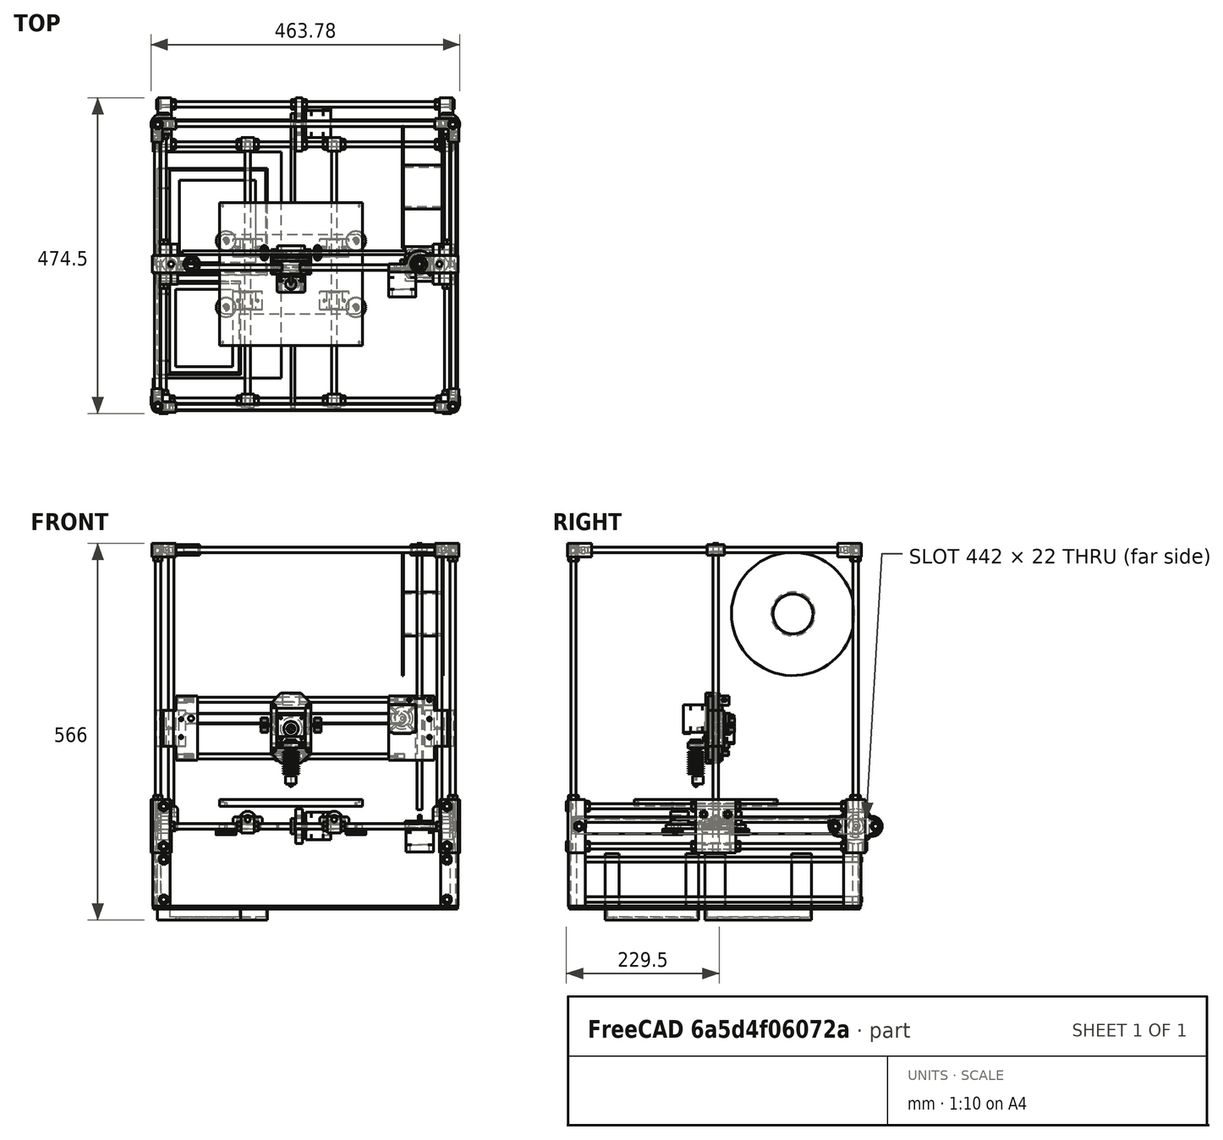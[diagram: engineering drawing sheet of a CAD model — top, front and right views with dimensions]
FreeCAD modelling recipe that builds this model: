
FCSTD DOCUMENT  (FreeCAD 0.16R6707 (Git))
Label: 3DPrinter
License: All rights reserved
LicenseURL: http://en.wikipedia.org/wiki/All_rights_reserved
objects: Part::Feature×127, Sketcher::SketchObject×20, PartDesign::Pad×20, Part::MultiFuse×16
note: 203 computed .brp shape members not serialized (recipe doc carries the construction recipe); baked Part::Feature solids carry a one-line shape summary decoded from their .brp

FEATURE [Sketcher::SketchObject] Sketch
  Placement = pos=(0,0,0) rot=(1,0,0;1.5708rad)
  sketch-geometry (2):
    g0: Circle CenterX=-65 CenterY=0 CenterZ=0 NormalX=0 NormalY=0 NormalZ=1 Radius=4
    g1: Circle CenterX=65 CenterY=0 CenterZ=0 NormalX=0 NormalY=0 NormalZ=1 Radius=4
  constraints (6):
    c: PointOnObject(g1,g-1)
    c: PointOnObject(g0,g-1)
    c: Radius(g0) = 4
    c: Equal(g0,g1)
    c: DistanceX(g0,g1) = 130
    c: Symmetric(g0,g1,g-2)
FEATURE [PartDesign::Pad] Pad  label="Rods"
  Length = 400
  Length2 = 100
  Midplane = true
  Placement = pos=(0,0,0) rot=(1,0,0;1.5708rad)
  Sketch = -> Sketch
  Type = 0
FEATURE [Sketcher::SketchObject] Sketch001
  Placement = pos=(0,0,-13.5) rot=(0,0,1;0rad)
  sketch-geometry (36):
    g0: LineSegment StartX=-97.5 StartY=60 StartZ=0 EndX=97.5 EndY=60 EndZ=0
    g1: LineSegment StartX=107.5 StartY=50 StartZ=0 EndX=107.5 EndY=-50 EndZ=0
    g2: LineSegment StartX=97.5 StartY=-60 StartZ=0 EndX=-97.5 EndY=-60 EndZ=0
    g3: LineSegment StartX=-107.5 StartY=-50 StartZ=0 EndX=-107.5 EndY=50 EndZ=0
    g4: ArcOfCircle CenterX=-97.5 CenterY=50 CenterZ=0 NormalX=0 NormalY=0 NormalZ=1 Radius=10 StartAngle=1.57079 EndAngle=3.14159
    g5: ArcOfCircle CenterX=97.5 CenterY=50 CenterZ=0 NormalX=0 NormalY=0 NormalZ=1 Radius=9.99998 StartAngle=6.28319 EndAngle=7.85398
    g6: ArcOfCircle CenterX=97.5 CenterY=-50 CenterZ=0 NormalX=0 NormalY=0 NormalZ=1 Radius=10 StartAngle=4.71239 EndAngle=6.28319
    g7: ArcOfCircle CenterX=-97.5 CenterY=-50 CenterZ=0 NormalX=0 NormalY=0 NormalZ=1 Radius=10 StartAngle=3.14159 EndAngle=4.71239
    g8: ArcOfCircle CenterX=-82.5 CenterY=40 CenterZ=0 NormalX=0 NormalY=0 NormalZ=1 Radius=1.8 StartAngle=1.5708 EndAngle=4.71239
    g9: ArcOfCircle CenterX=-77.5 CenterY=40 CenterZ=0 NormalX=0 NormalY=0 NormalZ=1 Radius=1.8 StartAngle=4.71239 EndAngle=7.85398
    g10: LineSegment StartX=-82.5 StartY=38.2 StartZ=0 EndX=-77.5 EndY=38.2 EndZ=0
    g11: LineSegment StartX=-82.5 StartY=41.8 StartZ=0 EndX=-77.5 EndY=41.8 EndZ=0
    g12: ArcOfCircle CenterX=-52.5 CenterY=40 CenterZ=0 NormalX=0 NormalY=0 NormalZ=1 Radius=1.8 StartAngle=1.5708 EndAngle=4.71239
    g13: ArcOfCircle CenterX=-47.5 CenterY=40 CenterZ=0 NormalX=0 NormalY=0 NormalZ=1 Radius=1.8 StartAngle=4.71239 EndAngle=7.85398
    g14: LineSegment StartX=-52.5 StartY=38.2 StartZ=0 EndX=-47.5 EndY=38.2 EndZ=0
    g15: LineSegment StartX=-52.5 StartY=41.8 StartZ=0 EndX=-47.5 EndY=41.8 EndZ=0
    g16: ArcOfCircle CenterX=47.5 CenterY=40 CenterZ=0 NormalX=0 NormalY=0 NormalZ=1 Radius=1.8 StartAngle=1.5708 EndAngle=4.71239
    g17: ArcOfCircle CenterX=52.5 CenterY=40 CenterZ=0 NormalX=0 NormalY=0 NormalZ=1 Radius=1.8 StartAngle=4.71239 EndAngle=7.85398
    g18: LineSegment StartX=47.5 StartY=38.2 StartZ=0 EndX=52.5 EndY=38.2 EndZ=0
    g19: LineSegment StartX=47.5 StartY=41.8 StartZ=0 EndX=52.5 EndY=41.8 EndZ=0
    g20: ArcOfCircle CenterX=77.5 CenterY=40 CenterZ=0 NormalX=0 NormalY=0 NormalZ=1 Radius=1.8 StartAngle=1.5708 EndAngle=4.71239
    g21: ArcOfCircle CenterX=82.5 CenterY=40 CenterZ=0 NormalX=0 NormalY=0 NormalZ=1 Radius=1.8 StartAngle=4.71239 EndAngle=7.85398
    g22: LineSegment StartX=77.5 StartY=38.2 StartZ=0 EndX=82.5 EndY=38.2 EndZ=0
    g23: LineSegment StartX=77.5 StartY=41.8 StartZ=0 EndX=82.5 EndY=41.8 EndZ=0
    g24: Circle CenterX=-80 CenterY=-40 CenterZ=0 NormalX=0 NormalY=0 NormalZ=1 Radius=1.8
    g25: Circle CenterX=-50 CenterY=-40 CenterZ=0 NormalX=0 NormalY=0 NormalZ=1 Radius=1.8
    g26: Circle CenterX=50 CenterY=-40 CenterZ=0 NormalX=0 NormalY=0 NormalZ=1 Radius=1.8
    g27: Circle CenterX=80 CenterY=-40 CenterZ=0 NormalX=0 NormalY=0 NormalZ=1 Radius=1.8
    g28: Circle CenterX=-97.5 CenterY=-50 CenterZ=0 NormalX=0 NormalY=0 NormalZ=1 Radius=1.8
    g29: Circle CenterX=-97.5 CenterY=50 CenterZ=0 NormalX=0 NormalY=0 NormalZ=1 Radius=1.8
    g30: Circle CenterX=97.5 CenterY=50 CenterZ=0 NormalX=0 NormalY=0 NormalZ=1 Radius=1.8
    g31: Circle CenterX=97.5 CenterY=-50 CenterZ=0 NormalX=0 NormalY=0 NormalZ=1 Radius=1.8
    g32: Circle CenterX=-20 CenterY=20 CenterZ=0 NormalX=0 NormalY=0 NormalZ=1 Radius=1.8
    g33: Circle CenterX=20 CenterY=20 CenterZ=0 NormalX=0 NormalY=0 NormalZ=1 Radius=1.8
    g34: Circle CenterX=-20 CenterY=-20 CenterZ=0 NormalX=0 NormalY=0 NormalZ=1 Radius=1.8
    g35: Circle CenterX=20 CenterY=-20 CenterZ=0 NormalX=0 NormalY=0 NormalZ=1 Radius=1.8
  constraints (95):
    c: Horizontal(g2)
    c: Vertical(g1)
    c: Vertical(g3)
    c: DistanceX(g0,g0) = 195
    c: DistanceY(g3,g3) = 100
    c: Symmetric(g0,g0,g-2)
    c: Symmetric(g2,g0,g-1)
    c: Coincident(g7,g3)
    c: Coincident(g7,g2)
    c: Coincident(g3,g4)
    c: Coincident(g4,g0)
    c: Coincident(g0,g5)
    c: Coincident(g5,g1)
    c: Coincident(g1,g6)
    c: Coincident(g6,g2)
    c: Tangent(g6,g1)
    c: Tangent(g5,g1)
    c: Tangent(g5,g0)
    c: Tangent(g2,g7)
    c: Tangent(g7,g3)
    c: Tangent(g3,g4)
    c: Tangent(g4,g0)
    c: Tangent(g6,g2)
    c: Equal(g4,g7)
    c: Equal(g7,g6)
    c: Radius(g4) = 10
    c: Tangent(g8,g11) = 1.5708
    c: Tangent(g8,g10) = -1.5708
    c: Tangent(g10,g9) = -1.5708
    c: Tangent(g11,g9) = 1.5708
    c: Horizontal(g10)
    c: Equal(g8,g9)
    c: Tangent(g12,g15) = 1.5708
    c: Tangent(g12,g14) = -1.5708
    c: Tangent(g14,g13) = -1.5708
    c: Tangent(g15,g13) = 1.5708
    c: Horizontal(g14)
    c: Equal(g12,g13)
    c: Tangent(g16,g19) = 1.5708
    c: Tangent(g16,g18) = -1.5708
    c: Tangent(g18,g17) = -1.5708
    c: Tangent(g19,g17) = 1.5708
    c: Horizontal(g18)
    c: Equal(g16,g17)
    c: Tangent(g20,g23) = 1.5708
    c: Tangent(g20,g22) = -1.5708
    c: Tangent(g22,g21) = -1.5708
    c: Tangent(g23,g21) = 1.5708
    c: Horizontal(g22)
    c: Equal(g20,g21)
    c: Radius(g24) = 1.8
    c: Equal(g24,g25)
    c: Equal(g24,g26)
    c: Equal(g24,g27)
    c: Equal(g24,g20)
    c: Equal(g24,g16)
    c: Equal(g24,g12)
    c: Equal(g24,g8)
    c: DistanceY(g25,g24) = 0
    c: DistanceY(g26,g25) = 0
    c: DistanceY(g26,g27) = 0
    c: DistanceY(g20,g17) = 0
    c: DistanceY(g16,g13) = 0
    c: DistanceY(g9,g12) = 0
    c: Symmetric(g13,g16,g-2)
    c: Symmetric(g25,g26,g-2)
    c: DistanceX(g24,g25) = 30
    c: DistanceX(g26,g27) = 30
    c: DistanceX(g25,g26) = 100
    c: DistanceX(g17,g20) = 25
    c: DistanceX(g16,g21) = 35
    c: Equal(g19,g23)
    c: Equal(g23,g15)
    c: Equal(g15,g11)
    c: DistanceX(g9,g12) = 25
    c: DistanceY(g8,g0) = 20
    c: DistanceY(g2,g24) = 20
    c: DistanceX(g13,g16) = 95
    c: Radius(g31) = 1.8
    c: Equal(g31,g30)
    c: Equal(g31,g29)
    c: Equal(g31,g28)
    c: Coincident(g28,g7)
    c: Coincident(g29,g4)
    c: Coincident(g30,g5)
    c: Coincident(g31,g6)
    c: Radius(g32) = 1.8
    c: Equal(g32,g33)
    c: Equal(g32,g34)
    c: Equal(g32,g35)
    c: Symmetric(g32,g33,g-2)
    c: Symmetric(g33,g35,g-1)
    c: Symmetric(g34,g32,g-1)
    c: DistanceX(g32,g33) = 40
    c: DistanceY(g34,g32) = 40
FEATURE [PartDesign::Pad] Pad001  label="Y-Base"
  Length = 6
  Length2 = 100
  Placement = pos=(0,0,-13.5) rot=(0,0,1;0rad)
  Sketch = -> Sketch001
  Type = 0
FEATURE [Part::Feature] Part__Feature  label="BearingMount001"
  Placement = pos=(65,-26,0) rot=(1,0,0;1.5708rad)
  shape: bbox 43.69 x 27 x 12.5 mm, 30 faces (baked)
FEATURE [Part::Feature] Part__Feature001  label="BearingMount002"
  Placement = pos=(65,53,0) rot=(1,0,0;1.5708rad)
  shape: bbox 43.69 x 27 x 12.5 mm, 30 faces (baked)
FEATURE [Part::Feature] Part__Feature002  label="BearingMount003"
  Placement = pos=(-65,-26,0) rot=(1,0,0;1.5708rad)
  shape: bbox 43.69 x 27 x 12.5 mm, 30 faces (baked)
FEATURE [Part::Feature] Part__Feature003  label="BearingMount004"
  Placement = pos=(-65,53,0) rot=(1,0,0;1.5708rad)
  shape: bbox 43.69 x 27 x 12.5 mm, 30 faces (baked)
FEATURE [Sketcher::SketchObject] Sketch002
  Placement = pos=(0,0,20) rot=(0,0,1;0rad)
  sketch-geometry (8):
    g0: LineSegment StartX=-107.5 StartY=107.5 StartZ=0 EndX=107.5 EndY=107.5 EndZ=0
    g1: LineSegment StartX=107.5 StartY=107.5 StartZ=0 EndX=107.5 EndY=-107.5 EndZ=0
    g2: LineSegment StartX=107.5 StartY=-107.5 StartZ=0 EndX=-107.5 EndY=-107.5 EndZ=0
    g3: LineSegment StartX=-107.5 StartY=-107.5 StartZ=0 EndX=-107.5 EndY=107.5 EndZ=0
    g4: Circle CenterX=-97.5 CenterY=-50 CenterZ=0 NormalX=0 NormalY=0 NormalZ=1 Radius=1.8
    g5: Circle CenterX=-97.5 CenterY=50 CenterZ=0 NormalX=0 NormalY=0 NormalZ=1 Radius=1.8
    g6: Circle CenterX=97.5 CenterY=-50 CenterZ=0 NormalX=0 NormalY=0 NormalZ=1 Radius=1.8
    g7: Circle CenterX=97.5 CenterY=50 CenterZ=0 NormalX=0 NormalY=0 NormalZ=1 Radius=1.8
  constraints (21):
    c: Coincident(g0,g1)
    c: Coincident(g1,g2)
    c: Coincident(g2,g3)
    c: Coincident(g3,g0)
    c: Horizontal(g0)
    c: Horizontal(g2)
    c: Vertical(g1)
    c: Vertical(g3)
    c: Symmetric(g1,g2,g-2)
    c: Symmetric(g0,g1,g-1)
    c: Equal(g1,g0)
    c: DistanceY(g1,g1) = 215
    c: Radius(g7) = 1.8
    c: Equal(g7,g6)
    c: Equal(g7,g5)
    c: Equal(g7,g4)
    c: Symmetric(g5,g7,g-2)
    c: Symmetric(g5,g4,g-1)
    c: Symmetric(g7,g6,g-1)
    c: DistanceX(g5,g7) = 195
    c: DistanceY(g4,g5) = 100
FEATURE [Part::Feature] Part__Feature004  label="BearingBase001"
  Placement = pos=(65,-53,0) rot=(-1,0,0;1.5708rad)
  shape: bbox 43.69 x 27 x 7.5 mm, 26 faces (baked)
FEATURE [Part::Feature] Part__Feature005  label="BearingBase002"
  Placement = pos=(65,26,0) rot=(-1,0,0;1.5708rad)
  shape: bbox 43.69 x 27 x 7.5 mm, 26 faces (baked)
FEATURE [Part::Feature] Part__Feature006  label="BearingBase003"
  Placement = pos=(-65,-53,0) rot=(-1,0,0;1.5708rad)
  shape: bbox 43.69 x 27 x 7.5 mm, 26 faces (baked)
FEATURE [Part::Feature] Part__Feature007  label="BearingBase004"
  Placement = pos=(-65,26,0) rot=(-1,0,0;1.5708rad)
  shape: bbox 43.69 x 27 x 7.5 mm, 26 faces (baked)
FEATURE [Part::MultiFuse] Fusion  label="BearingMount"
  Shapes = -> [Part__Feature007,Part__Feature,Part__Feature001,Part__Feature002,Part__Feature003,Part__Feature004,Part__Feature005,Part__Feature006]
FEATURE [PartDesign::Pad] Pad002  label="PrintingBedBase"
  Length = 5
  Length2 = 100
  Placement = pos=(0,0,20) rot=(0,0,1;0rad)
  Sketch = -> Sketch002
  Type = 0
FEATURE [Sketcher::SketchObject] Sketch003
  Placement = pos=(0,0,25) rot=(0,0,1;0rad)
  sketch-geometry (4):
    g0: LineSegment StartX=-107.5 StartY=107.5 StartZ=0 EndX=107.5 EndY=107.5 EndZ=0
    g1: LineSegment StartX=107.5 StartY=107.5 StartZ=0 EndX=107.5 EndY=-107.5 EndZ=0
    g2: LineSegment StartX=107.5 StartY=-107.5 StartZ=0 EndX=-107.5 EndY=-107.5 EndZ=0
    g3: LineSegment StartX=-107.5 StartY=-107.5 StartZ=0 EndX=-107.5 EndY=107.5 EndZ=0
  constraints (12):
    c: Coincident(g0,g1)
    c: Coincident(g1,g2)
    c: Coincident(g2,g3)
    c: Coincident(g3,g0)
    c: Horizontal(g0)
    c: Horizontal(g2)
    c: Vertical(g1)
    c: Vertical(g3)
    c: Symmetric(g1,g2,g-2)
    c: Symmetric(g0,g1,g-1)
    c: Equal(g1,g0)
    c: DistanceY(g1,g1) = 215
FEATURE [PartDesign::Pad] Pad003  label="Insulation"
  Length = 1
  Length2 = 100
  Placement = pos=(0,0,25) rot=(0,0,1;0rad)
  Sketch = -> Sketch003
  Type = 0
FEATURE [Sketcher::SketchObject] Sketch004
  Placement = pos=(0,0,26) rot=(0,0,1;0rad)
  sketch-geometry (8):
    g0: LineSegment StartX=-107.5 StartY=107.5 StartZ=0 EndX=107.5 EndY=107.5 EndZ=0
    g1: LineSegment StartX=107.5 StartY=107.5 StartZ=0 EndX=107.5 EndY=-107.5 EndZ=0
    g2: LineSegment StartX=107.5 StartY=-107.5 StartZ=0 EndX=-107.5 EndY=-107.5 EndZ=0
    g3: LineSegment StartX=-107.5 StartY=-107.5 StartZ=0 EndX=-107.5 EndY=107.5 EndZ=0
    g4: Circle CenterX=-102.5 CenterY=-102.5 CenterZ=0 NormalX=0 NormalY=0 NormalZ=1 Radius=1.3
    g5: Circle CenterX=-102.5 CenterY=102.5 CenterZ=0 NormalX=0 NormalY=0 NormalZ=1 Radius=1.3
    g6: Circle CenterX=102.5 CenterY=102.5 CenterZ=0 NormalX=0 NormalY=0 NormalZ=1 Radius=1.3
    g7: Circle CenterX=102.5 CenterY=-102.5 CenterZ=0 NormalX=0 NormalY=0 NormalZ=1 Radius=1.3
  constraints (21):
    c: Coincident(g0,g1)
    c: Coincident(g1,g2)
    c: Coincident(g2,g3)
    c: Coincident(g3,g0)
    c: Horizontal(g0)
    c: Horizontal(g2)
    c: Vertical(g1)
    c: Vertical(g3)
    c: Symmetric(g1,g2,g-2)
    c: Symmetric(g0,g1,g-1)
    c: Equal(g1,g0)
    c: DistanceY(g1,g1) = 215
    c: Radius(g5) = 1.3
    c: Equal(g5,g6)
    c: Equal(g5,g7)
    c: Equal(g5,g4)
    c: Symmetric(g4,g7,g-2)
    c: Symmetric(g7,g6,g-1)
    c: Symmetric(g5,g4,g-1)
    c: DistanceX(g5,g6) = 205
    c: DistanceY(g4,g5) = 205
FEATURE [PartDesign::Pad] Pad004  label="HeatBed"
  Length = 1
  Length2 = 100
  Placement = pos=(0,0,26) rot=(0,0,1;0rad)
  Sketch = -> Sketch004
  Type = 0
FEATURE [Sketcher::SketchObject] Sketch005
  Placement = pos=(0,0,27) rot=(0,0,1;0rad)
  sketch-geometry (4):
    g0: LineSegment StartX=-107.5 StartY=107.5 StartZ=0 EndX=107.5 EndY=107.5 EndZ=0
    g1: LineSegment StartX=107.5 StartY=107.5 StartZ=0 EndX=107.5 EndY=-107.5 EndZ=0
    g2: LineSegment StartX=107.5 StartY=-107.5 StartZ=0 EndX=-107.5 EndY=-107.5 EndZ=0
    g3: LineSegment StartX=-107.5 StartY=-107.5 StartZ=0 EndX=-107.5 EndY=107.5 EndZ=0
  constraints (12):
    c: Coincident(g0,g1)
    c: Coincident(g1,g2)
    c: Coincident(g2,g3)
    c: Coincident(g3,g0)
    c: Horizontal(g0)
    c: Horizontal(g2)
    c: Vertical(g1)
    c: Vertical(g3)
    c: Symmetric(g1,g2,g-2)
    c: Symmetric(g0,g1,g-1)
    c: Equal(g1,g0)
    c: DistanceY(g1,g1) = 215
FEATURE [PartDesign::Pad] Pad005  label="GlassPrintingBed"
  Length = 3
  Length2 = 100
  Placement = pos=(0,0,27) rot=(0,0,1;0rad)
  Sketch = -> Sketch005
  Type = 0
FEATURE [Part::Feature] Part__Feature008  label="HeightKnob001"
  Placement = pos=(97.5,-50,-22.5) rot=(0,0,1;0rad)
  shape: bbox 30 x 29.93 x 9 mm, 135 faces (baked)
FEATURE [Part::Feature] Part__Feature009  label="HeightKnob002"
  Placement = pos=(97.5,50,-22.5) rot=(0,0,1;0rad)
  shape: bbox 30 x 29.93 x 9 mm, 135 faces (baked)
FEATURE [Part::Feature] Part__Feature010  label="HeightKnob003"
  Placement = pos=(-97.5,-50,-22.5) rot=(0,0,1;0rad)
  shape: bbox 30 x 29.93 x 9 mm, 135 faces (baked)
FEATURE [Part::Feature] Part__Feature011  label="HeightKnob004"
  Placement = pos=(-97.5,50,-22.5) rot=(0,0,1;0rad)
  shape: bbox 30 x 29.93 x 9 mm, 135 faces (baked)
FEATURE [Part::MultiFuse] Fusion001  label="HeightKnob"
  Shapes = -> [Part__Feature008,Part__Feature009,Part__Feature010,Part__Feature011]
FEATURE [Part::MultiFuse] Fusion002  label="Y-Axis"
  Placement = pos=(0,0,15) rot=(0,0,1;0rad)
  Shapes = -> [Pad,Pad001,Fusion,Pad002,Pad003,Pad004,Pad005,Fusion001]
FEATURE [Part::Feature] Part__Feature012  label="Nema17"
  Placement = pos=(20.5,42.5,72) rot=(0,0.707107,-0.707107;3.14159rad)
  shape: bbox 41 x 55.5 x 43 mm, 73 faces (baked)
FEATURE [Part::Feature] Part__Feature013  label="Nema17_X"
  Placement = pos=(146.5,-34,87.5) rot=(-1,0,0;1.5708rad)
  shape: bbox 41 x 55.5 x 43 mm, 73 faces (baked)
FEATURE [Sketcher::SketchObject] Sketch006
  Placement = pos=(0,35,10) rot=(1,0,0;1.5708rad)
  sketch-geometry (20):
    g0: ArcOfCircle CenterX=-155 CenterY=57 CenterZ=0 NormalX=0 NormalY=0 NormalZ=1 Radius=7 StartAngle=1.5708 EndAngle=4.71239
    g1: ArcOfCircle CenterX=165 CenterY=57 CenterZ=0 NormalX=0 NormalY=0 NormalZ=1 Radius=7 StartAngle=4.71239 EndAngle=7.85398
    g2: LineSegment StartX=-155 StartY=64 StartZ=0 EndX=165 EndY=64 EndZ=0
    g3: ArcOfCircle CenterX=-155 CenterY=57 CenterZ=0 NormalX=0 NormalY=0 NormalZ=1 Radius=8 StartAngle=1.5708 EndAngle=4.71239
    g4: ArcOfCircle CenterX=165 CenterY=57 CenterZ=0 NormalX=0 NormalY=0 NormalZ=1 Radius=8 StartAngle=4.71239 EndAngle=7.85398
    g5: LineSegment StartX=-155 StartY=65 StartZ=0 EndX=165 EndY=65 EndZ=0
    g6: LineSegment StartX=165 StartY=50 StartZ=0 EndX=33.8479 EndY=50 EndZ=0
    g7: LineSegment StartX=33.8479 StartY=50 StartZ=0 EndX=33.8479 EndY=44 EndZ=0
    g8: LineSegment StartX=33.8479 StartY=44 StartZ=0 EndX=45.4113 EndY=44 EndZ=0
    g9: LineSegment StartX=45.4113 StartY=44 StartZ=0 EndX=45.4113 EndY=45 EndZ=0
    g10: LineSegment StartX=45.4113 StartY=45 StartZ=0 EndX=34.8479 EndY=45 EndZ=0
    g11: LineSegment StartX=34.8479 StartY=45 StartZ=0 EndX=34.8479 EndY=49 EndZ=0
    g12: LineSegment StartX=34.8479 StartY=49 StartZ=0 EndX=165 EndY=49 EndZ=0
    g13: LineSegment StartX=-155 StartY=50 StartZ=0 EndX=-33.8479 EndY=50 EndZ=0
    g14: LineSegment StartX=-34.8479 StartY=49 StartZ=0 EndX=-155 EndY=49 EndZ=0
    g15: LineSegment StartX=-33.8479 StartY=50 StartZ=0 EndX=-33.8479 EndY=44 EndZ=0
    g16: LineSegment StartX=-33.8479 StartY=44 StartZ=0 EndX=-45.4113 EndY=44 EndZ=0
    g17: LineSegment StartX=-45.4113 StartY=44 StartZ=0 EndX=-45.4113 EndY=45 EndZ=0
    g18: LineSegment StartX=-45.4113 StartY=45 StartZ=0 EndX=-34.8479 EndY=45 EndZ=0
    g19: LineSegment StartX=-34.8479 StartY=45 StartZ=0 EndX=-34.8479 EndY=49 EndZ=0
  constraints (56):
    c: Tangent(g0,g2) = 1.5708
    c: Tangent(g2,g1) = 1.5708
    c: Equal(g0,g1)
    c: Tangent(g3,g5) = 1.5708
    c: Tangent(g5,g4) = 1.5708
    c: Equal(g3,g4)
    c: Coincident(g1,g4)
    c: Coincident(g0,g3)
    c: Radius(g0) = 7
    c: Radius(g3) = 8
    c: DistanceY(g-1,g0) = 57
    c: DistanceX(g0,g1) = 320
    c: Horizontal(g6)
    c: Coincident(g6,g7)
    c: Vertical(g7)
    c: Coincident(g7,g8)
    c: Horizontal(g8)
    c: Coincident(g8,g9)
    c: Coincident(g9,g10)
    c: Horizontal(g10)
    c: Coincident(g10,g11)
    c: Vertical(g11)
    c: Coincident(g11,g12)
    c: Horizontal(g12)
    c: Vertical(g9)
    c: Coincident(g12,g4)
    c: Coincident(g6,g1)
    c: DistanceX(g6,g11) = 1
    c: DistanceY(g-1,g1) = 57
    c: Horizontal(g13)
    c: Horizontal(g14)
    c: Coincident(g13,g0)
    c: Coincident(g14,g3)
    c: Symmetric(g3,g3,g0)
    c: Symmetric(g0,g0,g0)
    c: Vertical(g15)
    c: Coincident(g15,g16)
    c: Coincident(g16,g17)
    c: Vertical(g17)
    c: Coincident(g17,g18)
    c: Horizontal(g18)
    c: Coincident(g18,g19)
    c: Vertical(g19)
    c: Horizontal(g16)
    c: Coincident(g19,g14)
    c: Coincident(g15,g13)
    c: DistanceX(g14,g13) = 1
    c: DistanceY(g17,g17) = 1
    c: DistanceY(g15,g13) = 6
    c: DistanceX(g-1,g1) = 165
    c: Equal(g16,g8)
    c: Equal(g15,g7)
    c: Equal(g19,g11)
    c: Equal(g17,g9)
    c: DistanceX(g13,g6) = 67.6959
    c: Symmetric(g13,g6,g-2)
FEATURE [PartDesign::Pad] Pad006  label="Belt"
  Length = 6
  Length2 = 100
  Placement = pos=(0,35,10) rot=(1,0,0;1.5708rad)
  Sketch = -> Sketch006
  Type = 0
FEATURE [Part::Feature] Part__Feature015  label="RBBeltTensioner"
  Placement = pos=(70,26,46) rot=(0,0,1;0rad)
  shape: bbox 10 x 22 x 8 mm, 25 faces (baked)
FEATURE [Part::Feature] Part__Feature016  label="RBeltClip"
  Placement = pos=(70,26,55) rot=(0,0,1;0rad)
  shape: bbox 10 x 22 x 4 mm, 8 faces (baked)
FEATURE [Part::Feature] Part__Feature017  label="RTBeltTensioner"
  Placement = pos=(70,38,68) rot=(1,0,0;3.14159rad)
  shape: bbox 10 x 22 x 8 mm, 25 faces (baked)
FEATURE [Part::MultiFuse] Fusion003  label="RBeltGrip"
  Placement = pos=(-30,0,0) rot=(0,0,1;0rad)
  Shapes = -> [Part__Feature015,Part__Feature016,Part__Feature017]
FEATURE [Part::Feature] Part__Feature020  label="RBBeltTensioner001"
  Placement = pos=(70,26,46) rot=(0,0,1;0rad)
  shape: bbox 10 x 22 x 8 mm, 25 faces (baked)
FEATURE [Part::Feature] Part__Feature021  label="RBeltClip001"
  Placement = pos=(70,26,55) rot=(0,0,1;0rad)
  shape: bbox 10 x 22 x 4 mm, 8 faces (baked)
FEATURE [Part::Feature] Part__Feature022  label="RTBeltTensioner001"
  Placement = pos=(70,38,68) rot=(1,0,0;3.14159rad)
  shape: bbox 10 x 22 x 8 mm, 25 faces (baked)
FEATURE [Part::Feature] Part__Feature024  label="Spring"
  Placement = pos=(-10.5,27,115) rot=(0,0,1;0rad)
  shape: bbox 13.99 x 15.54 x 13.93 mm, 6 faces, 0 solids (baked)
FEATURE [Part::Feature] Part__Feature025  label="HotEnd"
  Placement = pos=(0,-15,-36) rot=(0,0,1;0rad)
  shape: bbox 24 x 24 x 70.5 mm, 70 faces (baked)
FEATURE [Part::Feature] Part__Feature026  label="Lever"
  Placement = pos=(9,-15,23) rot=(0,0,1;0rad)
  shape: bbox 42 x 50 x 17 mm, 46 faces (baked)
FEATURE [Part::Feature] Part__Feature027  label="HotEndMount"
  Placement = pos=(51,-15,23) rot=(0,0,1;3.14159rad)
  shape: bbox 42 x 12 x 8 mm, 18 faces (baked)
FEATURE [Part::Feature] Part__Feature029  label="FrontPanel"
  Placement = pos=(-30,0,105) rot=(-1,0,0;1.5708rad)
  shape: bbox 60 x 15 x 105 mm, 69 faces (baked)
FEATURE [Part::Feature] Part__Feature030  label="BackPanel"
  Placement = pos=(-30,20,0) rot=(1,0,0;1.5708rad)
  shape: bbox 60 x 10 x 105 mm, 53 faces (baked)
FEATURE [Part::MultiFuse] Fusion004  label="HotEndMount001"
  Placement = pos=(-30,0,0) rot=(0,0,1;0rad)
  Shapes = -> [Part__Feature027,Part__Feature026]
FEATURE [Part::Feature] Part__Feature034  label="RDoubleLinearBearingMount"
  Placement = pos=(223,15,25.5) rot=(0,0,1;0rad)
  shape: bbox 43.69 x 12.5 x 54 mm, 40 faces (baked)
FEATURE [Part::Feature] Part__Feature037  label="LeadScrewNutMount"
  Placement = pos=(193,15,87) rot=(0,0,1;0rad)
  shape: bbox 40 x 20 x 14 mm, 28 faces (baked)
FEATURE [Part::Feature] Part__Feature038  label="LDoubleLinearBearingMount"
  Placement = pos=(-180,15,25.5) rot=(0,0,1;0rad)
  shape: bbox 43.69 x 12.5 x 54 mm, 40 faces (baked)
FEATURE [Part::Feature] Part__Feature039  label="LShoulder"
  Placement = pos=(-180,15,4) rot=(0,0,1;0rad)
  shape: bbox 61.84 x 12.5 x 97 mm, 53 faces (baked)
FEATURE [Part::Feature] Part__Feature040  label="RShoulder"
  Placement = pos=(223,15,4) rot=(0,0,1;0rad)
  shape: bbox 98.34 x 12 x 97 mm, 91 faces (baked)
FEATURE [Sketcher::SketchObject] Sketch007
  Placement = pos=(0,0,0) rot=(0.57735,0.57735,0.57735;2.0944rad)
  sketch-geometry (2):
    g0: Circle CenterX=10 CenterY=95 CenterZ=0 NormalX=0 NormalY=0 NormalZ=1 Radius=4
    g1: Circle CenterX=10 CenterY=10 CenterZ=0 NormalX=0 NormalY=0 NormalZ=1 Radius=4
  constraints (6):
    c: DistanceX(g1,g0) = 0
    c: Radius(g0) = 4
    c: Equal(g0,g1)
    c: DistanceX(g-1,g0) = 10
    c: DistanceY(g1,g0) = 85
    c: DistanceY(g-1,g1) = 10
FEATURE [PartDesign::Pad] Pad007  label="X-Rods"
  Length = 340
  Length2 = 100
  Midplane = true
  Placement = pos=(0,0,0) rot=(0.57735,0.57735,0.57735;2.0944rad)
  Sketch = -> Sketch007
  Type = 0
FEATURE [Part::MultiFuse] Fusion005  label="Shoulder"
  Shapes = -> [Part__Feature039,Part__Feature038,Part__Feature037,Part__Feature034,Part__Feature040]
FEATURE [Part::MultiFuse] Fusion006  label="LBeltGrip"
  Placement = pos=(-110,0,0) rot=(0,0,1;0rad)
  Shapes = -> [Part__Feature020,Part__Feature021,Part__Feature022]
FEATURE [Sketcher::SketchObject] Sketch008
  Placement = pos=(0,0,30) rot=(0,0,1;0rad)
  sketch-geometry (3):
    g0: Circle CenterX=-180 CenterY=15 CenterZ=0 NormalX=0 NormalY=0 NormalZ=1 Radius=4
    g1: Circle CenterX=193 CenterY=15 CenterZ=0 NormalX=0 NormalY=0 NormalZ=1 Radius=4
    g2: Circle CenterX=223 CenterY=15 CenterZ=0 NormalX=0 NormalY=0 NormalZ=1 Radius=4
  constraints (9):
    c: Radius(g2) = 4
    c: Equal(g2,g1)
    c: Equal(g2,g0)
    c: DistanceY(g1,g0) = 0
    c: DistanceY(g1,g2) = 0
    c: DistanceX(g1) = 193
    c: DistanceX(g1,g2) = 30
    c: DistanceX(g0,g2) = 403
    c: DistanceY(g-1,g1) = 15
FEATURE [PartDesign::Pad] Pad008  label="Z-Rods"
  Length = 400
  Length2 = 100
  Placement = pos=(0,0,30) rot=(0,0,1;0rad)
  Sketch = -> Sketch008
  Type = 0
FEATURE [Part::Feature] Part__Feature043  label="FrameMountL"
  Placement = pos=(232.6,20.6,-35) rot=(0,0,-1;1.5708rad)
  shape: bbox 22 x 60 x 80 mm, 28 faces (baked)
FEATURE [Part::Feature] Part__Feature045  label="AxisMountL"
  Placement = pos=(219,16.75,0) rot=(0,0,1;1.5708rad)
  shape: bbox 52 x 60 x 35 mm, 38 faces (baked)
FEATURE [Part::Feature] Part__Feature046  label="Nema17-Z"
  Placement = pos=(173,-5,-33.5) rot=(0,0,1;0rad)
  shape: bbox 41 x 43 x 55.5 mm, 73 faces (baked)
FEATURE [Part::Feature] Part__Feature044  label="FrameMountR"
  Placement = pos=(-189.6,9.4,-35) rot=(0,0,1;1.5708rad)
  shape: bbox 22 x 60 x 80 mm, 28 faces (baked)
FEATURE [Sketcher::SketchObject] Sketch009
  Placement = pos=(0,20,0) rot=(1,0,0;1.5708rad)
  sketch-geometry (4):
    g0: Circle CenterX=234.5 CenterY=35 CenterZ=0 NormalX=0 NormalY=0 NormalZ=1 Radius=4
    g1: Circle CenterX=234.5 CenterY=-25 CenterZ=0 NormalX=0 NormalY=0 NormalZ=1 Radius=4
    g2: Circle CenterX=-191.3 CenterY=35 CenterZ=0 NormalX=0 NormalY=0 NormalZ=1 Radius=4
    g3: Circle CenterX=-191.3 CenterY=-25 CenterZ=0 NormalX=0 NormalY=0 NormalZ=1 Radius=4
  constraints (12):
    c: Radius(g3) = 4
    c: Equal(g3,g2)
    c: Equal(g3,g1)
    c: Equal(g3,g0)
    c: DistanceX(g0,g1) = 0
    c: DistanceY(g-1,g0) = 35
    c: DistanceY(g1,g0) = 60
    c: DistanceX(g-1,g0) = 234.5
    c: DistanceY(g2,g0) = 0
    c: DistanceX(g3,g2) = 0
    c: DistanceY(g3,g2) = 60
    c: DistanceX(g2,g0) = 425.8
FEATURE [PartDesign::Pad] Pad009  label="FrameRods001"
  Length = 440
  Length2 = 100
  Midplane = true
  Placement = pos=(0,20,0) rot=(1,0,0;1.5708rad)
  Sketch = -> Sketch009
  Type = 0
FEATURE [Sketcher::SketchObject] Sketch010
  Placement = pos=(-201,0,0) rot=(0.57735,0.57735,0.57735;2.0944rad)
  sketch-geometry (3):
    g0: Circle CenterX=-190.3 CenterY=5 CenterZ=0 NormalX=0 NormalY=0 NormalZ=1 Radius=4
    g1: Circle CenterX=194.908 CenterY=5 CenterZ=0 NormalX=0 NormalY=0 NormalZ=1 Radius=4
    g2: Circle CenterX=254.908 CenterY=5 CenterZ=0 NormalX=0 NormalY=0 NormalZ=1 Radius=4
  constraints (8):
    c: Radius(g0) = 4
    c: DistanceY(g0,g-1) = -5
    c: DistanceX(g0,g-1) = 190.3
    c: Radius(g1) = 4
    c: DistanceY(g0,g1) = 0
    c: Equal(g1,g2)
    c: DistanceY(g2,g1) = 0
    c: DistanceX(g1,g2) = 60
FEATURE [PartDesign::Pad] Pad010  label="FrameRods002"
  Length = 446
  Length2 = 100
  Placement = pos=(-201,0,0) rot=(0.57735,0.57735,0.57735;2.0944rad)
  Sketch = -> Sketch010
  Type = 0
FEATURE [Sketcher::SketchObject] Sketch011
  Placement = pos=(0,0,15) rot=(0.57735,0.57735,0.57735;2.0944rad)
  sketch-geometry (8):
    g0: ArcOfCircle CenterX=-190 CenterY=-10 CenterZ=0 NormalX=0 NormalY=0 NormalZ=1 Radius=11 StartAngle=1.5708 EndAngle=4.71239
    g1: ArcOfCircle CenterX=230 CenterY=-10 CenterZ=0 NormalX=0 NormalY=0 NormalZ=1 Radius=11 StartAngle=4.71239 EndAngle=7.85398
    g2: LineSegment StartX=-190 StartY=-21 StartZ=0 EndX=230 EndY=-21 EndZ=0
    g3: LineSegment StartX=-190 StartY=1 StartZ=0 EndX=230 EndY=1 EndZ=0
    g4: ArcOfCircle CenterX=-190 CenterY=-10 CenterZ=0 NormalX=0 NormalY=0 NormalZ=1 Radius=11.5 StartAngle=1.5708 EndAngle=4.71239
    g5: ArcOfCircle CenterX=230 CenterY=-10 CenterZ=0 NormalX=0 NormalY=0 NormalZ=1 Radius=11.5 StartAngle=4.71239 EndAngle=7.85398
    g6: LineSegment StartX=-190 StartY=-21.5 StartZ=0 EndX=230 EndY=-21.5 EndZ=0
    g7: LineSegment StartX=-190 StartY=1.5 StartZ=0 EndX=230 EndY=1.5 EndZ=0
  constraints (19):
    c: Tangent(g0,g3) = 1.5708
    c: Tangent(g0,g2) = -1.5708
    c: Tangent(g2,g1) = -1.5708
    c: Tangent(g3,g1) = 1.5708
    c: Horizontal(g2)
    c: Equal(g0,g1)
    c: Tangent(g4,g7) = 1.5708
    c: Tangent(g4,g6) = -1.5708
    c: Tangent(g6,g5) = -1.5708
    c: Tangent(g7,g5) = 1.5708
    c: Horizontal(g6)
    c: Equal(g4,g5)
    c: Coincident(g0,g4)
    c: Coincident(g5,g1)
    c: Radius(g1) = 11
    c: Radius(g5) = 11.5
    c: DistanceY(g0,g-1) = 10
    c: DistanceX(g0,g-1) = 190
    c: DistanceX(g0,g1) = 420
FEATURE [PartDesign::Pad] Pad011  label="Y-Belt"
  Length = 6
  Length2 = 100
  Placement = pos=(0,0,15) rot=(0.57735,0.57735,0.57735;2.0944rad)
  Sketch = -> Sketch011
  Type = 0
FEATURE [Part::Feature] Part__Feature047  label="Nema17-Y"
  Placement = pos=(59.5,205,-15) rot=(0,-1,0;1.5708rad)
  shape: bbox 55.5 x 43 x 41 mm, 73 faces (baked)
FEATURE [Part::Feature] Part__Feature056  label="AxisMountR"
  Placement = pos=(-175.645,13.24,0) rot=(0,0,-1;1.5708rad)
  shape: bbox 10 x 60 x 35 mm, 11 faces (baked)
FEATURE [Part::MultiFuse] Fusion012  label="AxisMount"
  Shapes = -> [Part__Feature056,Part__Feature045]
FEATURE [Sketcher::SketchObject] Sketch012
  Placement = pos=(0,0,0) rot=(0.57735,0.57735,0.57735;2.0944rad)
  sketch-geometry (2):
    g0: Circle CenterX=138.947 CenterY=143.911 CenterZ=0 NormalX=0 NormalY=0 NormalZ=1 Radius=92.5
    g1: Circle CenterX=138.947 CenterY=143.911 CenterZ=0 NormalX=0 NormalY=0 NormalZ=1 Radius=30
  constraints (3):
    c: Coincident(g1,g0)
    c: Radius(g0) = 92.5
    c: Radius(g1) = 30
FEATURE [PartDesign::Pad] Pad012
  Length = 2
  Length2 = 100
  Placement = pos=(0,0,0) rot=(0.57735,0.57735,0.57735;2.0944rad)
  Sketch = -> Sketch012
  Type = 0
FEATURE [Sketcher::SketchObject] Sketch013
  Placement = pos=(60,0,0) rot=(0.57735,0.57735,0.57735;2.0944rad)
  sketch-geometry (2):
    g0: Circle CenterX=138.947 CenterY=143.911 CenterZ=0 NormalX=0 NormalY=0 NormalZ=1 Radius=92.5
    g1: Circle CenterX=138.947 CenterY=143.911 CenterZ=0 NormalX=0 NormalY=0 NormalZ=1 Radius=30
  constraints (3):
    c: Coincident(g1,g0)
    c: Radius(g0) = 92.5
    c: Radius(g1) = 30
FEATURE [PartDesign::Pad] Pad013
  Length = 2
  Length2 = 100
  Placement = pos=(60,0,0) rot=(0.57735,0.57735,0.57735;2.0944rad)
  Sketch = -> Sketch013
  Type = 0
FEATURE [Sketcher::SketchObject] Sketch014
  Placement = pos=(2,0,0) rot=(0.57735,0.57735,0.57735;2.0944rad)
  sketch-geometry (2):
    g0: Circle CenterX=138.95 CenterY=144.13 CenterZ=0 NormalX=0 NormalY=0 NormalZ=1 Radius=30
    g1: Circle CenterX=138.95 CenterY=144.13 CenterZ=0 NormalX=0 NormalY=0 NormalZ=1 Radius=33
  constraints (3):
    c: Coincident(g0,g1)
    c: Radius(g0) = 30
    c: Radius(g1) = 33
FEATURE [PartDesign::Pad] Pad014
  Length = 58
  Length2 = 100
  Placement = pos=(2,0,0) rot=(0.57735,0.57735,0.57735;2.0944rad)
  Sketch = -> Sketch014
  Type = 0
FEATURE [Part::MultiFuse] Fusion014  label="PlasticRole"
  Placement = pos=(167,-8,180) rot=(0,0,1;0rad)
  Shapes = -> [Pad012,Pad013,Pad014]
FEATURE [Sketcher::SketchObject] Sketch015
  Placement = pos=(0,-177.5,0) rot=(1,0,0;1.5708rad)
  sketch-geometry (2):
    g0: Circle CenterX=-200.8 CenterY=420 CenterZ=0 NormalX=0 NormalY=0 NormalZ=1 Radius=4
    g1: Circle CenterX=244 CenterY=420 CenterZ=0 NormalX=0 NormalY=0 NormalZ=1 Radius=4
  constraints (6):
    c: Radius(g0) = 4
    c: Equal(g0,g1)
    c: DistanceY(g0,g1) = 0
    c: DistanceX(g0,g1) = 444.8
    c: DistanceY(g-1,g0) = 420
    c: DistanceX(g0,g-1) = 200.8
FEATURE [PartDesign::Pad] Pad015  label="CasingRods001"
  Length = 380
  Length2 = 100
  Placement = pos=(0,-177.5,0) rot=(1,0,0;1.5708rad)
  Reversed = true
  Sketch = -> Sketch015
  Type = 0
FEATURE [Sketcher::SketchObject] Sketch016
  Placement = pos=(22,0,0) rot=(0.57735,0.57735,0.57735;2.0944rad)
  sketch-geometry (2):
    g0: Circle CenterX=-199.8 CenterY=420 CenterZ=0 NormalX=0 NormalY=0 NormalZ=1 Radius=4
    g1: Circle CenterX=225.9 CenterY=420 CenterZ=0 NormalX=0 NormalY=0 NormalZ=1 Radius=4
  constraints (6):
    c: Radius(g1) = 4
    c: Equal(g1,g0)
    c: DistanceY(g0,g1) = 0
    c: DistanceY(g-1,g0) = 420
    c: DistanceX(g0,g1) = 425.7
    c: DistanceX(g0,g-1) = 199.8
FEATURE [PartDesign::Pad] Pad016  label="CasingRods002"
  Length = 400
  Length2 = 100
  Midplane = true
  Placement = pos=(22,0,0) rot=(0.57735,0.57735,0.57735;2.0944rad)
  Sketch = -> Sketch016
  Type = 0
FEATURE [Sketcher::SketchObject] Sketch017
  Placement = pos=(7,-55,0) rot=(0,0,1;0rad)
  sketch-geometry (4):
    g0: Circle CenterX=-206.8 CenterY=279.9 CenterZ=0 NormalX=0 NormalY=0 NormalZ=1 Radius=4
    g1: Circle CenterX=236 CenterY=279.9 CenterZ=0 NormalX=0 NormalY=0 NormalZ=1 Radius=4
    g2: Circle CenterX=-206.8 CenterY=-143.8 CenterZ=0 NormalX=0 NormalY=0 NormalZ=1 Radius=4
    g3: Circle CenterX=236 CenterY=-143.8 CenterZ=0 NormalX=0 NormalY=0 NormalZ=1 Radius=4
  constraints (12):
    c: Radius(g1) = 4
    c: Equal(g1,g0)
    c: DistanceY(g1,g0) = 0
    c: DistanceX(g0,g1) = 442.8
    c: DistanceX(g0,g-1) = 206.8
    c: DistanceY(g-1,g0) = 279.9
    c: Radius(g2) = 4
    c: Equal(g2,g3)
    c: DistanceX(g2,g-1) = 206.8
    c: DistanceX(g2,g3) = 442.8
    c: DistanceY(g3,g2) = 0
    c: DistanceY(g3,g-1) = 143.8
FEATURE [PartDesign::Pad] Pad017  label="CasingRodsBack"
  Length = 430
  Length2 = 100
  Placement = pos=(7,-55,0) rot=(0,0,1;0rad)
  Sketch = -> Sketch017
  Type = 0
FEATURE [Part::Feature] Part__Feature064  label="Corner_FL"
  Placement = pos=(238,-193.8,45) rot=(0.707107,0.707107,0;3.14159rad)
  shape: bbox 26 x 26 x 80 mm, 32 faces (baked)
FEATURE [Part::Feature] Part__Feature065  label="Corner_FR"
  Placement = pos=(-194.8,-193.8,-35) rot=(0,0,1;1.5708rad)
  shape: bbox 26 x 26 x 80 mm, 32 faces (baked)
FEATURE [Part::Feature] Part__Feature067  label="Corner_BR"
  Placement = pos=(-194.8,224.9,-35) rot=(0,0,1;1.5708rad)
  shape: bbox 30.43 x 80 x 80 mm, 51 faces (baked)
FEATURE [Part::Feature] Part__Feature068  label="Corner_BL"
  Placement = pos=(238,224.9,-35) rot=(0,0,-1;1.5708rad)
  shape: bbox 30.43 x 80 x 80 mm, 51 faces (baked)
FEATURE [Part::MultiFuse] Fusion015  label="Frame"
  Shapes = -> [Part__Feature067,Part__Feature046,Fusion012,Part__Feature068,Pad009,Pad010,Part__Feature044,Part__Feature043,Part__Feature064,Part__Feature065]
FEATURE [Part::Feature] Part__Feature069  label="Y_MotorMount"
  Placement = pos=(17,225,5) rot=(0.57735,-0.57735,-0.57735;2.0944rad)
  shape: bbox 10 x 80 x 52 mm, 17 faces (baked)
FEATURE [Part::Feature] Part__Feature070  label="RodMount001"
  Placement = pos=(65,195,5) rot=(0,0,1;0rad)
  shape: bbox 10 x 20 x 25 mm, 10 faces (baked)
FEATURE [Part::Feature] Part__Feature071  label="RodMount002"
  Placement = pos=(65,-190.3,5) rot=(0,0,1;0rad)
  shape: bbox 10 x 20 x 25 mm, 10 faces (baked)
FEATURE [Part::Feature] Part__Feature072  label="RodMount003"
  Placement = pos=(-65,195,5) rot=(0,0,1;0rad)
  shape: bbox 10 x 20 x 25 mm, 10 faces (baked)
FEATURE [Part::Feature] Part__Feature073  label="RodMount004"
  Placement = pos=(-65,-190.3,5) rot=(0,0,1;0rad)
  shape: bbox 10 x 20 x 25 mm, 10 faces (baked)
FEATURE [Part::Feature] Part__Feature074  label="RodMountI001"
  Placement = pos=(65,195,5) rot=(0,0,1;3.14159rad)
  shape: bbox 10 x 20 x 25 mm, 10 faces (baked)
FEATURE [Part::Feature] Part__Feature075  label="RodMountI002"
  Placement = pos=(65,-190.3,5) rot=(0,0,1;3.14159rad)
  shape: bbox 10 x 20 x 25 mm, 10 faces (baked)
FEATURE [Part::Feature] Part__Feature076  label="RodMountI003"
  Placement = pos=(-65,195,5) rot=(0,0,1;3.14159rad)
  shape: bbox 10 x 20 x 25 mm, 10 faces (baked)
FEATURE [Part::Feature] Part__Feature077  label="RodMountI004"
  Placement = pos=(-65,-190.3,5) rot=(0,0,1;3.14159rad)
  shape: bbox 10 x 20 x 25 mm, 10 faces (baked)
FEATURE [Part::MultiFuse] Fusion016  label="Y-Axis_Mount"
  Shapes = -> [Part__Feature069,Part__Feature070,Part__Feature071,Part__Feature072,Part__Feature073,Part__Feature074,Part__Feature075,Part__Feature076,Part__Feature077]
FEATURE [Part::Feature] Part__Feature078  label="M8_001"
  Placement = pos=(0.5,195,5) rot=(0,1,0;1.5708rad)
  shape: bbox 6.5 x 15 x 15 mm, 29 faces (baked)
FEATURE [Part::Feature] Part__Feature079  label="M8_002"
  Placement = pos=(0.5,255,5) rot=(0,1,0;1.5708rad)
  shape: bbox 6.5 x 15 x 15 mm, 29 faces (baked)
FEATURE [Part::Feature] Part__Feature080  label="M8_003"
  Placement = pos=(17,195,5) rot=(0,1,0;1.5708rad)
  shape: bbox 6.5 x 15 x 15 mm, 29 faces (baked)
FEATURE [Part::Feature] Part__Feature081  label="M8_004"
  Placement = pos=(17,255,5) rot=(0,1,0;1.5708rad)
  shape: bbox 6.5 x 15 x 15 mm, 29 faces (baked)
FEATURE [Part::Feature] Part__Feature082  label="M8_005"
  Placement = pos=(-55,195,5) rot=(0,1,0;1.5708rad)
  shape: bbox 6.5 x 15 x 15 mm, 29 faces (baked)
FEATURE [Part::Feature] Part__Feature083  label="M8_006"
  Placement = pos=(75,195,5) rot=(0,1,0;1.5708rad)
  shape: bbox 6.5 x 15 x 15 mm, 29 faces (baked)
FEATURE [Part::Feature] Part__Feature084  label="M8_007"
  Placement = pos=(48.5,195,5) rot=(0,1,0;1.5708rad)
  shape: bbox 6.5 x 15 x 15 mm, 29 faces (baked)
FEATURE [Part::Feature] Part__Feature085  label="M8_008"
  Placement = pos=(-81.5,195,5) rot=(0,1,0;1.5708rad)
  shape: bbox 6.5 x 15 x 15 mm, 29 faces (baked)
FEATURE [Part::Feature] Part__Feature086  label="M8_009"
  Placement = pos=(-202,195,5) rot=(0,1,0;1.5708rad)
  shape: bbox 6.5 x 15 x 15 mm, 29 faces (baked)
FEATURE [Part::Feature] Part__Feature087  label="M8_010"
  Placement = pos=(-180,195,5) rot=(0,1,0;1.5708rad)
  shape: bbox 6.5 x 15 x 15 mm, 29 faces (baked)
FEATURE [Part::Feature] Part__Feature088  label="M8_011"
  Placement = pos=(-180,255,5) rot=(0,1,0;1.5708rad)
  shape: bbox 6.5 x 15 x 15 mm, 29 faces (baked)
FEATURE [Part::Feature] Part__Feature089  label="M8_012"
  Placement = pos=(-202,255,5) rot=(0,1,0;1.5708rad)
  shape: bbox 6.5 x 15 x 15 mm, 29 faces (baked)
FEATURE [Part::Feature] Part__Feature090  label="M8_013"
  Placement = pos=(216.5,255,5) rot=(0,1,0;1.5708rad)
  shape: bbox 6.5 x 15 x 15 mm, 29 faces (baked)
FEATURE [Part::Feature] Part__Feature091  label="M8_014"
  Placement = pos=(239,255,5) rot=(0,1,0;1.5708rad)
  shape: bbox 6.5 x 15 x 15 mm, 29 faces (baked)
FEATURE [Part::Feature] Part__Feature092  label="M8_015"
  Placement = pos=(216.5,195,5) rot=(0,1,0;1.5708rad)
  shape: bbox 6.5 x 15 x 15 mm, 29 faces (baked)
FEATURE [Part::Feature] Part__Feature093  label="M8_016"
  Placement = pos=(239,195,5) rot=(0,1,0;1.5708rad)
  shape: bbox 6.5 x 15 x 15 mm, 29 faces (baked)
FEATURE [Part::Feature] Part__Feature094  label="M8_017"
  Placement = pos=(247,-190.3,5) rot=(0.242937,0.940428,0.237857;1.62709rad)
  shape: bbox 6.593 x 15.03 x 15.02 mm, 29 faces (baked)
FEATURE [Part::Feature] Part__Feature095  label="M8_018"
  Placement = pos=(-210,-190.3,5) rot=(0.242937,0.940428,0.237857;1.62709rad)
  shape: bbox 6.593 x 15.03 x 15.02 mm, 29 faces (baked)
FEATURE [Part::Feature] Part__Feature096  label="M8_019"
  Placement = pos=(218.5,-190.3,5) rot=(0,1,0;1.5708rad)
  shape: bbox 6.5 x 15 x 15 mm, 29 faces (baked)
FEATURE [Part::Feature] Part__Feature097  label="M8_020"
  Placement = pos=(-55,-190.3,5) rot=(0,1,0;1.5708rad)
  shape: bbox 6.5 x 15 x 15 mm, 29 faces (baked)
FEATURE [Part::Feature] Part__Feature098  label="M8_021"
  Placement = pos=(48.5,-190.3,5) rot=(0,1,0;1.5708rad)
  shape: bbox 6.5 x 15 x 15 mm, 29 faces (baked)
FEATURE [Part::Feature] Part__Feature099  label="M8_022"
  Placement = pos=(75,-190.3,5) rot=(0,1,0;1.5708rad)
  shape: bbox 6.5 x 15 x 15 mm, 29 faces (baked)
FEATURE [Part::Feature] Part__Feature100  label="M8_023"
  Placement = pos=(-81.5,-190.3,5) rot=(0,1,0;1.5708rad)
  shape: bbox 6.5 x 15 x 15 mm, 29 faces (baked)
FEATURE [Part::Feature] Part__Feature101  label="M8_024"
  Placement = pos=(-181.5,-190.3,5) rot=(0,1,0;1.5708rad)
  shape: bbox 6.5 x 15 x 15 mm, 29 faces (baked)
FEATURE [Part::Feature] Part__Feature102  label="M8_025"
  Placement = pos=(243,224.9,45) rot=(0,0,1;0rad)
  shape: bbox 15 x 15 x 6.5 mm, 29 faces (baked)
FEATURE [Part::Feature] Part__Feature103  label="M8_026"
  Placement = pos=(-199.8,224.9,45) rot=(0,0,1;0rad)
  shape: bbox 15 x 15 x 6.5 mm, 29 faces (baked)
FEATURE [Part::Feature] Part__Feature104  label="M8_027"
  Placement = pos=(-199.8,-198.8,45) rot=(0,0,1;0rad)
  shape: bbox 15 x 15 x 6.5 mm, 29 faces (baked)
FEATURE [Part::Feature] Part__Feature105  label="M8_028"
  Placement = pos=(243,-198.8,45) rot=(0,0,1;0rad)
  shape: bbox 15 x 15 x 6.5 mm, 29 faces (baked)
FEATURE [Part::Feature] Part__Feature106  label="M8_029_TC"
  Placement = pos=(243,224.9,403.5) rot=(0,0,1;0rad)
  shape: bbox 15 x 15 x 6.5 mm, 29 faces (baked)
FEATURE [Part::Feature] Part__Feature107  label="M8_030_TC"
  Placement = pos=(-199.8,224.9,403.5) rot=(0,0,1;0rad)
  shape: bbox 15 x 15 x 6.5 mm, 29 faces (baked)
FEATURE [Part::Feature] Part__Feature108  label="M8_031_TC"
  Placement = pos=(-199.8,-198.8,403.5) rot=(0,0,1;0rad)
  shape: bbox 15 x 15 x 6.5 mm, 29 faces (baked)
FEATURE [Part::Feature] Part__Feature109  label="M8_032_TC"
  Placement = pos=(243,-198.8,403.5) rot=(0,0,1;0rad)
  shape: bbox 15 x 15 x 6.5 mm, 29 faces (baked)
FEATURE [Part::Feature] Part__Feature110  label="M8_029_TC001"
  Placement = pos=(243,224.9,423) rot=(0,0,1;0rad)
  shape: bbox 15 x 15 x 6.5 mm, 29 faces (baked)
FEATURE [Part::Feature] Part__Feature111  label="M8_030_TC001"
  Placement = pos=(-199.8,224.9,423) rot=(0,0,1;0rad)
  shape: bbox 15 x 15 x 6.5 mm, 29 faces (baked)
FEATURE [Part::Feature] Part__Feature112  label="M8_031_TC001"
  Placement = pos=(-199.8,-198.8,423) rot=(0,0,1;0rad)
  shape: bbox 15 x 15 x 6.5 mm, 29 faces (baked)
FEATURE [Part::Feature] Part__Feature113  label="M8_032_TC001"
  Placement = pos=(243,-198.8,423) rot=(0,0,1;0rad)
  shape: bbox 15 x 15 x 6.5 mm, 29 faces (baked)
FEATURE [Part::Feature] Part__Feature114  label="M8_029"
  Placement = pos=(234.5,-203,-25) rot=(1,0,0;1.5708rad)
  shape: bbox 15 x 6.5 x 15 mm, 29 faces (baked)
FEATURE [Part::Feature] Part__Feature115  label="M8_030"
  Placement = pos=(234.5,-174.5,35) rot=(1,0,0;1.5708rad)
  shape: bbox 15 x 6.5 x 15 mm, 29 faces (baked)
FEATURE [Part::Feature] Part__Feature116  label="M8_031"
  Placement = pos=(-191.3,-203,-25) rot=(1,0,0;1.5708rad)
  shape: bbox 15 x 6.5 x 15 mm, 29 faces (baked)
FEATURE [Part::Feature] Part__Feature117  label="M8_032"
  Placement = pos=(-191.3,-203,35) rot=(1,0,0;1.5708rad)
  shape: bbox 15 x 6.5 x 15 mm, 29 faces (baked)
FEATURE [Part::Feature] Part__Feature118  label="M8_033"
  Placement = pos=(234.5,-174.5,-25) rot=(1,0,0;1.5708rad)
  shape: bbox 15 x 6.5 x 15 mm, 29 faces (baked)
FEATURE [Part::Feature] Part__Feature119  label="M8_034"
  Placement = pos=(234.5,51.5,-25) rot=(1,0,0;1.5708rad)
  shape: bbox 15 x 6.5 x 15 mm, 29 faces (baked)
FEATURE [Part::Feature] Part__Feature120  label="M8_035"
  Placement = pos=(234.5,-15,-25) rot=(1,0,0;1.5708rad)
  shape: bbox 15 x 6.5 x 15 mm, 29 faces (baked)
FEATURE [Part::Feature] Part__Feature121  label="M8_036"
  Placement = pos=(234.5,210,-25) rot=(1,0,0;1.5708rad)
  shape: bbox 15 x 6.5 x 15 mm, 29 faces (baked)
FEATURE [Part::Feature] Part__Feature122  label="M8_037"
  Placement = pos=(234.5,242,-25) rot=(0.935051,-0.250678,0.250678;1.6379rad)
  shape: bbox 15 x 6.5 x 15 mm, 29 faces (baked)
FEATURE [Part::Feature] Part__Feature123  label="M8_038"
  Placement = pos=(234.5,242,35) rot=(0.935051,-0.250678,0.250678;1.6379rad)
  shape: bbox 15 x 6.5 x 15 mm, 29 faces (baked)
FEATURE [Part::Feature] Part__Feature124  label="M8_039"
  Placement = pos=(-191.3,242,35) rot=(0.935051,-0.250678,0.250678;1.6379rad)
  shape: bbox 15 x 6.5 x 15 mm, 29 faces (baked)
FEATURE [Part::Feature] Part__Feature125  label="M8_040"
  Placement = pos=(-191.3,242,-25) rot=(0.935051,-0.250678,0.250678;1.6379rad)
  shape: bbox 15 x 6.5 x 15 mm, 29 faces (baked)
FEATURE [Part::Feature] Part__Feature126  label="M8_041"
  Placement = pos=(-191.3,-174.5,-25) rot=(1,0,0;1.5708rad)
  shape: bbox 15 x 6.5 x 15 mm, 29 faces (baked)
FEATURE [Part::Feature] Part__Feature127  label="M8_042"
  Placement = pos=(-191.3,-15,-25) rot=(1,0,0;1.5708rad)
  shape: bbox 15 x 6.5 x 15 mm, 29 faces (baked)
FEATURE [Part::Feature] Part__Feature128  label="M8_043"
  Placement = pos=(-191.3,51.5,-25) rot=(1,0,0;1.5708rad)
  shape: bbox 15 x 6.5 x 15 mm, 29 faces (baked)
FEATURE [Part::Feature] Part__Feature129  label="M8_044"
  Placement = pos=(-191.3,210,-25) rot=(1,0,0;1.5708rad)
  shape: bbox 15 x 6.5 x 15 mm, 29 faces (baked)
FEATURE [Part::Feature] Part__Feature130  label="M8_045"
  Placement = pos=(-191.3,-174.5,35) rot=(1,0,0;1.5708rad)
  shape: bbox 15 x 6.5 x 15 mm, 29 faces (baked)
FEATURE [Part::Feature] Part__Feature131  label="M8_046"
  Placement = pos=(-191.3,-15,35) rot=(1,0,0;1.5708rad)
  shape: bbox 15 x 6.5 x 15 mm, 29 faces (baked)
FEATURE [Part::Feature] Part__Feature132  label="M8_047"
  Placement = pos=(-191.3,51.5,35) rot=(1,0,0;1.5708rad)
  shape: bbox 15 x 6.5 x 15 mm, 29 faces (baked)
FEATURE [Part::Feature] Part__Feature133  label="M8_048"
  Placement = pos=(-191.3,210,35) rot=(1,0,0;1.5708rad)
  shape: bbox 15 x 6.5 x 15 mm, 29 faces (baked)
FEATURE [Part::Feature] Part__Feature134  label="M8_049"
  Placement = pos=(234.5,-203,35) rot=(1,0,0;1.5708rad)
  shape: bbox 15 x 6.5 x 15 mm, 29 faces (baked)
FEATURE [Part::Feature] Part__Feature135  label="M8_050"
  Placement = pos=(234.5,-15,35) rot=(1,0,0;1.5708rad)
  shape: bbox 15 x 6.5 x 15 mm, 29 faces (baked)
FEATURE [Part::Feature] Part__Feature136  label="M8_051"
  Placement = pos=(234.5,51.5,35) rot=(1,0,0;1.5708rad)
  shape: bbox 15 x 6.5 x 15 mm, 29 faces (baked)
FEATURE [Part::Feature] Part__Feature137  label="M8_052"
  Placement = pos=(234.5,210,35) rot=(1,0,0;1.5708rad)
  shape: bbox 15 x 6.5 x 15 mm, 29 faces (baked)
FEATURE [Part::MultiFuse] Fusion017  label="M8Nuts"
  Shapes = -> [Part__Feature102,Part__Feature078,Part__Feature079,Part__Feature080,Part__Feature081,Part__Feature082,Part__Feature083,Part__Feature084,Part__Feature085,Part__Feature086,Part__Feature087,Part__Feature088,Part__Feature089,Part__Feature090,Part__Feature091,Part__Feature092,Part__Feature093,Part__Feature094,Part__Feature095,Part__Feature096,Part__Feature097,Part__Feature098,Part__Feature099,+37 more]
FEATURE [Part::Feature] Part__Feature138  label="Corner_Bottom_FR"
  Placement = pos=(-199.8,-198.8,410) rot=(0,0,1;0rad)
  shape: bbox 36 x 36 x 12.5 mm, 41 faces (baked)
FEATURE [Part::Feature] Part__Feature140  label="Corner_Top_FR"
  Placement = pos=(-199.8,-198.8,430) rot=(0.707107,0.707107,0;3.14159rad)
  shape: bbox 36 x 36 x 10 mm, 48 faces (baked)
FEATURE [Part::Feature] Part__Feature141  label="Corner_Bottom_FL"
  Placement = pos=(243,-198.8,410) rot=(0,0,1;1.5708rad)
  shape: bbox 36 x 36 x 12.5 mm, 41 faces (baked)
FEATURE [Part::Feature] Part__Feature142  label="Corner_Top_FL"
  Placement = pos=(243,-198.8,430) rot=(0,1,0;3.14159rad)
  shape: bbox 36 x 36 x 10 mm, 48 faces (baked)
FEATURE [Part::Feature] Part__Feature143  label="Corner_Bottom_BL"
  Placement = pos=(243,224.9,410) rot=(0,0,1;3.14159rad)
  shape: bbox 36 x 36 x 12.5 mm, 41 faces (baked)
FEATURE [Part::Feature] Part__Feature144  label="Corner_Top_BL"
  Placement = pos=(243,224.9,430) rot=(0.707107,-0.707107,0;3.14159rad)
  shape: bbox 36 x 36 x 10 mm, 48 faces (baked)
FEATURE [Part::Feature] Part__Feature145  label="Corner_Bottom_BR"
  Placement = pos=(-199.8,224.9,410) rot=(0,0,-1;1.5708rad)
  shape: bbox 36 x 36 x 12.5 mm, 41 faces (baked)
FEATURE [Part::Feature] Part__Feature146  label="Corner_Top_BR"
  Placement = pos=(-199.8,224.9,430) rot=(1,0,0;3.14159rad)
  shape: bbox 36 x 36 x 10 mm, 48 faces (baked)
FEATURE [Part::Feature] Part__Feature148  label="FrameRodMount_L"
  Placement = pos=(223,15,412) rot=(0,0,1;0rad)
  shape: bbox 71 x 26 x 16 mm, 13 faces (baked)
FEATURE [Part::Feature] Part__Feature149  label="FrameRodMount_R"
  Placement = pos=(-180,15,412) rot=(0,0,1;3.14159rad)
  shape: bbox 71 x 26 x 16 mm, 13 faces (baked)
FEATURE [Part::MultiFuse] Fusion018  label="TopFrame"
  Shapes = -> [Part__Feature138,Part__Feature140,Part__Feature141,Part__Feature142,Part__Feature143,Part__Feature144,Part__Feature145,Part__Feature146,Part__Feature148,Part__Feature149]
FEATURE [Part::Feature] Part__Feature150  label="Peripheral001"
  Placement = pos=(30,20,11.25) rot=(0,0.707107,0.707107;3.14159rad)
  shape: bbox 60 x 17 x 88 mm, 127 faces (baked)
FEATURE [Part::MultiFuse] Fusion019  label="X_Carrage"
  Shapes = -> [Part__Feature150,Fusion006,Part__Feature030,Part__Feature029,Fusion003]
FEATURE [Part::MultiFuse] Fusion020
  Placement = pos=(0,0,100) rot=(0,0,1;0rad)
  Shapes = -> [Fusion019,Part__Feature012,Part__Feature025,Part__Feature013,Fusion005,Pad007,Fusion004,Pad006]
FEATURE [Part::Feature] Part__Feature151  label="PCB"
  Placement = pos=(86,-100,-21) rot=(0,0,1;0rad)
  shape: bbox 125 x 140 x 100 mm, 24 faces (baked)
FEATURE [Part::Feature] Part__Feature152  label="Cut"
  Placement = pos=(432.8,-213.7,80) rot=(0.707107,0.707107,0;3.14159rad)
  shape: bbox 26 x 26 x 80 mm, 24 faces (baked)
FEATURE [Part::Feature] Part__Feature153  label="PSU"
  Placement = pos=(86,50,-21) rot=(0,0,1;0rad)
  shape: bbox 165 x 160 x 100 mm, 24 faces (baked)
FEATURE [Part::Feature] Part__Feature154  label="Cut003"
  Placement = pos=(0,-213.7,0) rot=(0,0,1;1.5708rad)
  shape: bbox 26 x 26 x 80 mm, 24 faces (baked)
FEATURE [Part::Feature] Part__Feature155  label="Cut004"
  Placement = pos=(0,200,80) rot=(0.708549,-0.705662,0;3.14159rad)
  shape: bbox 26.07 x 26.11 x 80 mm, 24 faces (baked)
FEATURE [Part::Feature] Part__Feature156  label="Cut005"
  Placement = pos=(432.8,200,0) rot=(0,0,-1;1.5708rad)
  shape: bbox 26 x 26 x 80 mm, 24 faces (baked)
FEATURE [Sketcher::SketchObject] Sketch018
  Placement = pos=(194.8,-6,35) rot=(1,0,0;1.5708rad)
  sketch-geometry (4):
    g0: Circle CenterX=234.5 CenterY=35 CenterZ=0 NormalX=0 NormalY=0 NormalZ=1 Radius=4
    g1: Circle CenterX=234.5 CenterY=-25 CenterZ=0 NormalX=0 NormalY=0 NormalZ=1 Radius=4
    g2: Circle CenterX=-191.3 CenterY=35 CenterZ=0 NormalX=0 NormalY=0 NormalZ=1 Radius=4
    g3: Circle CenterX=-191.3 CenterY=-25 CenterZ=0 NormalX=0 NormalY=0 NormalZ=1 Radius=4
  constraints (12):
    c: Radius(g3) = 4
    c: Equal(g3,g2)
    c: Equal(g3,g1)
    c: Equal(g3,g0)
    c: DistanceX(g0,g1) = 0
    c: DistanceY(g-1,g0) = 35
    c: DistanceY(g1,g0) = 60
    c: DistanceX(g-1,g0) = 234.5
    c: DistanceY(g2,g0) = 0
    c: DistanceX(g3,g2) = 0
    c: DistanceY(g3,g2) = 60
    c: DistanceX(g2,g0) = 425.8
FEATURE [PartDesign::Pad] Pad018  label="FrameRods003"
  Length = 440
  Length2 = 100
  Midplane = true
  Placement = pos=(194.8,-6,35) rot=(1,0,0;1.5708rad)
  Sketch = -> Sketch018
  Type = 0
FEATURE [Sketcher::SketchObject] Sketch019
  Placement = pos=(0,0,-4) rot=(0,0,1;0rad)
  sketch-geometry (12):
    g0: LineSegment StartX=-12 StartY=212 StartZ=0 EndX=445 EndY=212 EndZ=0
    g1: LineSegment StartX=445 StartY=212 StartZ=0 EndX=445 EndY=-225 EndZ=0
    g2: LineSegment StartX=445 StartY=-225 StartZ=0 EndX=-12 EndY=-225 EndZ=0
    g3: LineSegment StartX=-12 StartY=-225 StartZ=0 EndX=-12 EndY=-176.5 EndZ=0
    g4: LineSegment StartX=-12 StartY=-176.5 StartZ=0 EndX=180 EndY=-176.5 EndZ=0
    g5: LineSegment StartX=180 StartY=-176.5 StartZ=0 EndX=180 EndY=163.5 EndZ=0
    g6: LineSegment StartX=180 StartY=163.5 StartZ=0 EndX=-12 EndY=163.5 EndZ=0
    g7: LineSegment StartX=-12 StartY=163.5 StartZ=0 EndX=-12 EndY=212 EndZ=0
    g8: Circle CenterX=-5 CenterY=-218.7 CenterZ=0 NormalX=0 NormalY=0 NormalZ=1 Radius=4
    g9: Circle CenterX=437.8 CenterY=-218.7 CenterZ=0 NormalX=0 NormalY=0 NormalZ=1 Radius=4
    g10: Circle CenterX=437.8 CenterY=205 CenterZ=0 NormalX=0 NormalY=0 NormalZ=1 Radius=4
    g11: Circle CenterX=-5 CenterY=205 CenterZ=0 NormalX=0 NormalY=0 NormalZ=1 Radius=4
  constraints (37):
    c: Horizontal(g0)
    c: Coincident(g0,g1)
    c: Vertical(g1)
    c: Coincident(g1,g2)
    c: Horizontal(g2)
    c: Coincident(g2,g3)
    c: Vertical(g3)
    c: Coincident(g3,g4)
    c: Horizontal(g4)
    c: Coincident(g4,g5)
    c: Vertical(g5)
    c: Coincident(g5,g6)
    c: Horizontal(g6)
    c: Coincident(g6,g7)
    c: Coincident(g7,g0)
    c: Vertical(g7)
    c: Equal(g6,g4)
    c: Equal(g0,g2)
    c: Equal(g3,g7)
    c: DistanceX(g-1,g5) = 180
    c: DistanceX(g-1,g0) = 445
    c: DistanceY(g1,g1) = 437
    c: DistanceY(g-1,g0) = 212
    c: DistanceX(g3,g-1) = 12
    c: DistanceY(g5,g5) = 340
    c: Radius(g11) = 4
    c: Equal(g11,g8)
    c: Equal(g11,g9)
    c: Equal(g11,g10)
    c: DistanceX(g11,g-1) = 5
    c: DistanceY(g-1,g11) = 205
    c: DistanceY(g10,g11) = 0
    c: DistanceX(g-1,g10) = 437.8
    c: DistanceX(g8,g-1) = 5
    c: DistanceY(g8,g9) = 0
    c: DistanceX(g9,g10) = 0
    c: DistanceY(g8,g-1) = 218.7
FEATURE [PartDesign::Pad] Pad019  label="Plexi"
  Length = 4
  Length2 = 100
  Placement = pos=(0,0,-4) rot=(0,0,1;0rad)
  Sketch = -> Sketch019
  Type = 0
FEATURE [Part::MultiFuse] Fusion021
  Placement = pos=(-194.8,20,-115) rot=(0,0,1;0rad)
  Shapes = -> [Pad019,Part__Feature151,Part__Feature152,Part__Feature153,Part__Feature154,Part__Feature155,Part__Feature156,Pad018]
